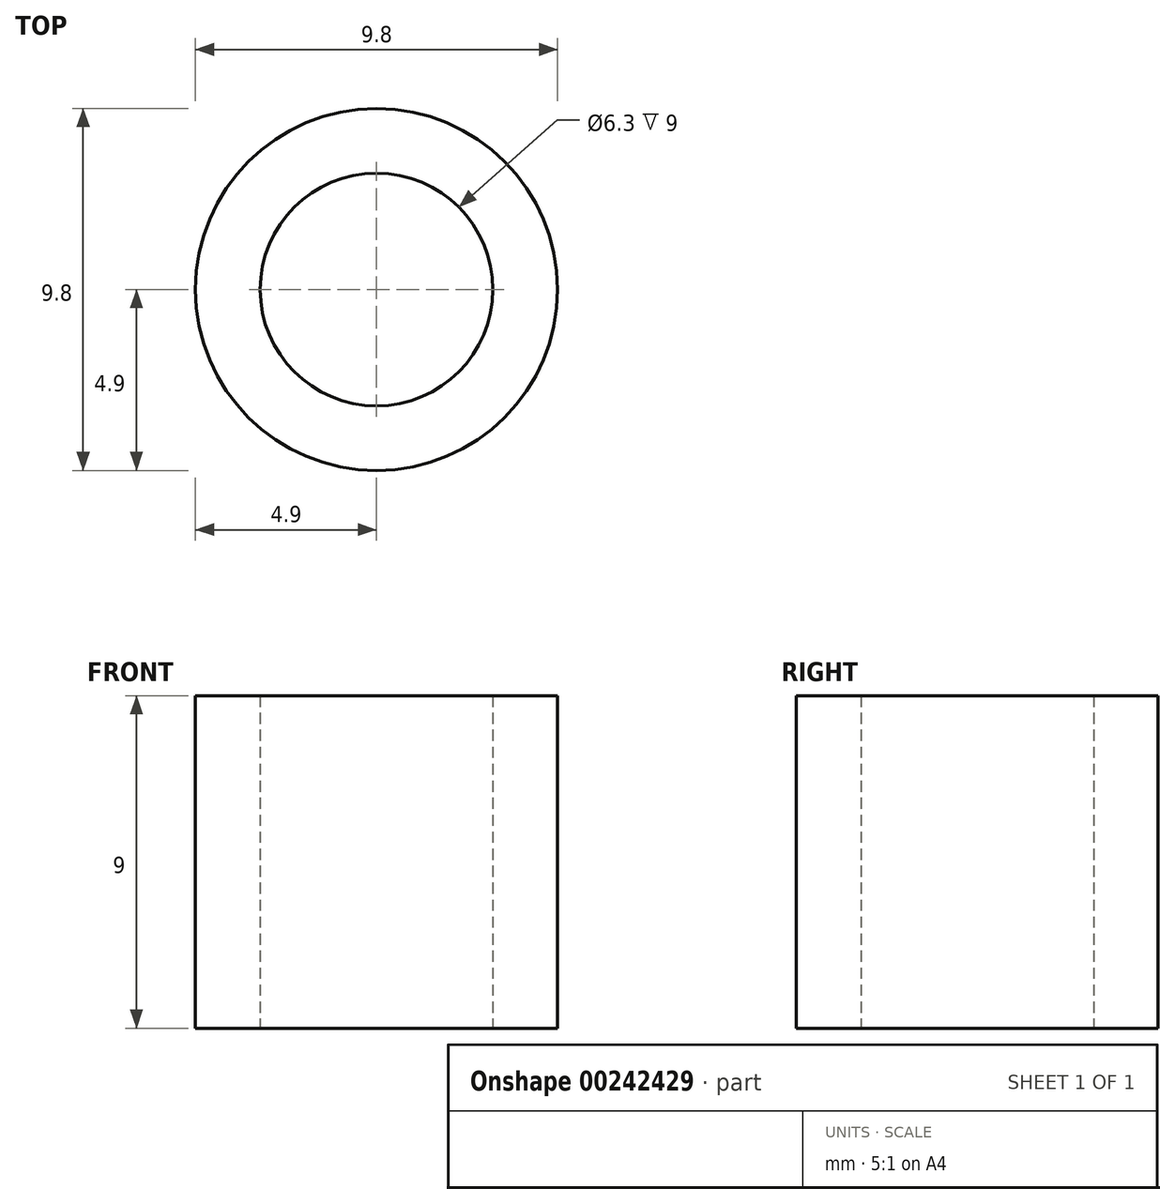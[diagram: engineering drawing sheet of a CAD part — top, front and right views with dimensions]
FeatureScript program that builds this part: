
annotation { "Feature Type Name" : "Feature", "Feature Type Description" : "" }
export const myFeature = defineFeature(function(context is Context, id is Id, definition is map)
    precondition{}
    {
        {
            var Q0;
            Q0=qCreatedBy(makeId("Top.planeOp"),FACE);
            var sketch = newSketch(context, id + "F0", { "sketchPlane" : qUnion([Q0])});
            skCircle(sketch, "E0", {"center": v(0, 0) * mm, "radius": 3.15 * mm});
            skCircle(sketch, "E1", {"center": v(0, 0) * mm, "radius": 4.9 * mm});
            skSolve(sketch);
        }
        {
            var Q0;
            Q0=makeQuery(id+"F0.imprint","IMPRINT",FACE,{"disambiguationData":[TD([[makeQuery(id+"F0.imprint","IMPRINT",EDGE,{"derivedFrom":sQuery(id+"F0.wireOp",EDGE,"E0")}),-1.0]])]});
            extrude(context, id + "F1", {"entities" : qUnion([Q0]), "depth" : 9 * mm, "offsetDistance" : 25 * mm});
        }
    });
